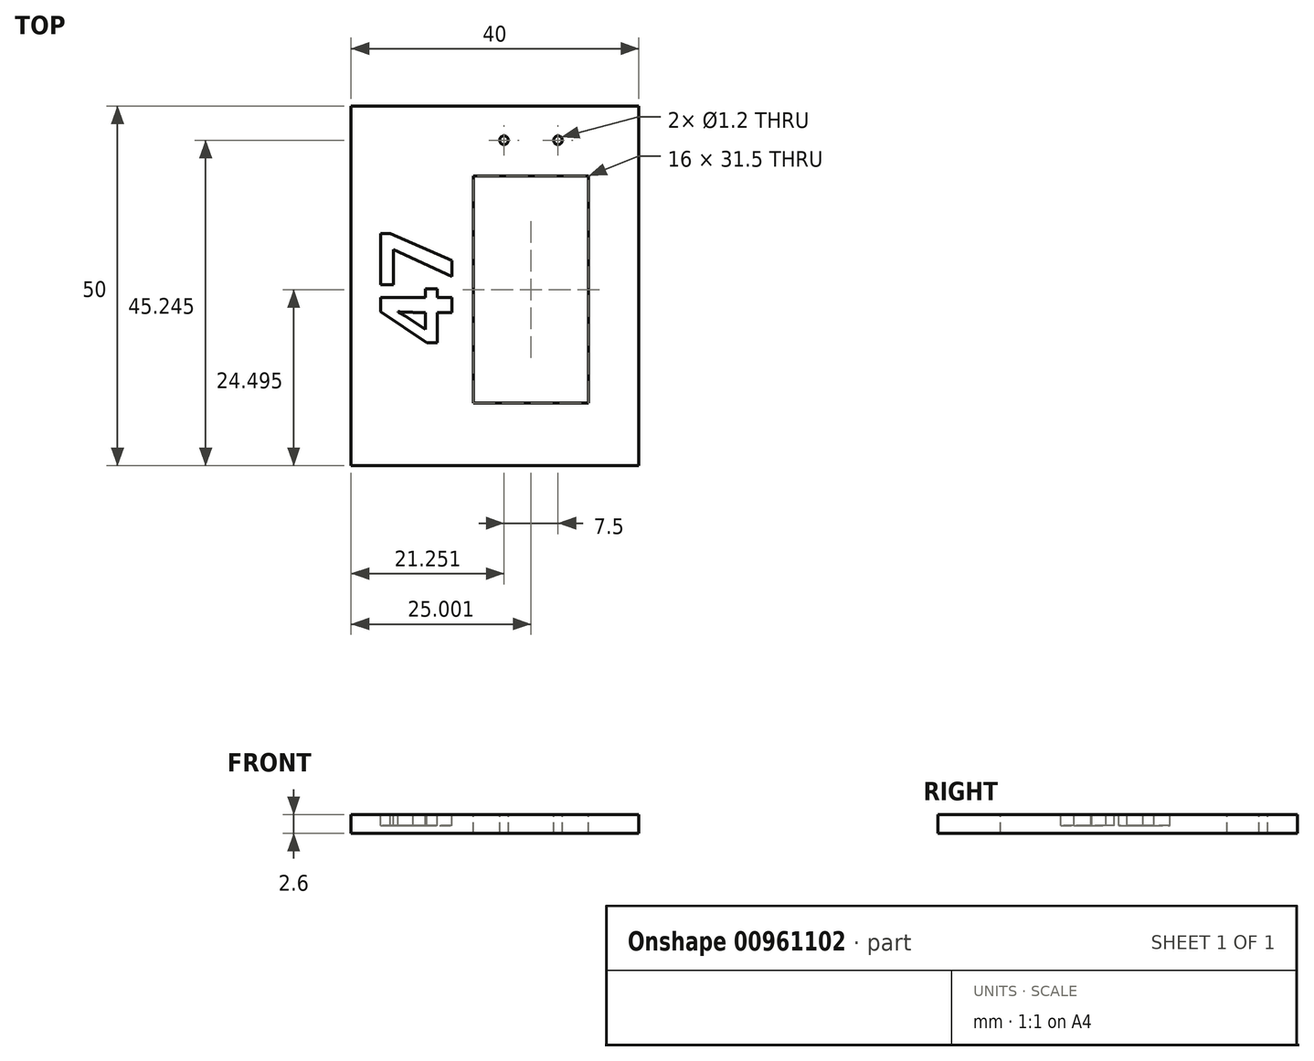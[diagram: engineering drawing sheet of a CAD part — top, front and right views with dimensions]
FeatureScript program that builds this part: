
annotation { "Feature Type Name" : "Feature", "Feature Type Description" : "" }
export const myFeature = defineFeature(function(context is Context, id is Id, definition is map)
    precondition{}
    {
        {
            var Q0;
            Q0=qCreatedBy(makeId("Top.planeOp"),FACE);
            var sketch = newSketch(context, id + "F0", { "sketchPlane" : qUnion([Q0])});
            skLineSegment(sketch, "E0.bottom", {"start": v(-43.16, 28.34) * mm, "end": v(-3.16, 28.34) * mm});
            skLineSegment(sketch, "E0.top", {"start": v(-43.16, -21.66) * mm, "end": v(-3.16, -21.66) * mm});
            skLineSegment(sketch, "E0.left", {"start": v(-43.16, 28.34) * mm, "end": v(-43.16, -21.66) * mm});
            skLineSegment(sketch, "E0.right", {"start": v(-3.16, 28.34) * mm, "end": v(-3.16, -21.66) * mm});
            skSolve(sketch);
        }
        {
            var Q0;
            Q0=makeQuery(id+"F0.imprint","IMPRINT",FACE,{"disambiguationData":[TD([[makeQuery(id+"F0.imprint","IMPRINT",EDGE,{"derivedFrom":sQuery(id+"F0.wireOp",EDGE,"E0.bottom")}),-1.0]])]});
            extrude(context, id + "F1", {"entities" : qUnion([Q0]), "depth" : 2.6 * mm, "offsetDistance" : 25 * mm});
        }
        {
            var Q0;
            Q0=makeQuery(id+"F1.opExtrude","CAP_FACE",FACE,{"disambiguationData":[OSD([sQuery(id+"F0.wireOp",EDGE,"E0.bottom"),sQuery(id+"F0.wireOp",EDGE,"E0.top"),sQuery(id+"F0.wireOp",EDGE,"E0.left"),sQuery(id+"F0.wireOp",EDGE,"E0.right")])],"isStart":false});
            var sketch = newSketch(context, id + "F2", { "sketchPlane" : qUnion([Q0])});
            skText(sketch, "E1", { "text": "47", "fontName": "OpenSans-Bold.ttf"});
            const initialGuessF2  = {"E1": [-0.02916, -0.00481, 0, 1, 0.01]};
            skSetInitialGuess(sketch, initialGuessF2);
            skSolve(sketch);
        }
        {
            var Q0;
            Q0=qSketchRegion(id+"F2",true);
            extrude(context, id + "F3", {"entities" : qUnion([Q0]), "operationType" : NewBodyOperationType.REMOVE, "oppositeDirection" : true, "depth" : 1.5 * mm, "offsetDistance" : 25 * mm});
        }
        {
            var Q0;
            {var subQ0=sQuery(id+"F0.wireOp",EDGE,"E0.left");var subQ1=sQuery(id+"F0.wireOp",EDGE,"E0.bottom");var subQ2=sQuery(id+"F0.wireOp",EDGE,"E0.right");var subQ3=sQuery(id+"F0.wireOp",EDGE,"E0.top");Q0=makeQuery(id+"F3.boolean.opBoolean","SPLIT",FACE,{"disambiguationData":[TD([makeQuery(id+"F1.opExtrude","SWEPT_FACE",FACE,{"disambiguationData":[OSD([subQ1])]})])],"derivedFrom":makeQuery(id+"F1.opExtrude","CAP_FACE",FACE,{"disambiguationData":[OSD([subQ1,subQ3,subQ0,subQ2])],"isStart":false})});}
            var sketch = newSketch(context, id + "F4", { "sketchPlane" : qUnion([Q0])});
            skLineSegment(sketch, "E2.bottom", {"start": v(-26.16, -12.91) * mm, "end": v(-10.16, -12.91) * mm});
            skLineSegment(sketch, "E2.top", {"start": v(-26.16, 18.59) * mm, "end": v(-10.16, 18.59) * mm});
            skLineSegment(sketch, "E2.left", {"start": v(-26.16, -12.91) * mm, "end": v(-26.16, 18.59) * mm});
            skLineSegment(sketch, "E2.right", {"start": v(-10.16, -12.91) * mm, "end": v(-10.16, 18.59) * mm});
            skCircle(sketch, "E3", {"center": v(-21.9, 23.59) * mm, "radius": 0.6 * mm});
            skCircle(sketch, "E4", {"center": v(-14.4, 23.59) * mm, "radius": 0.6 * mm});
            skSolve(sketch);
        }
        {
            var Q0;
            Q0 = qSketchRegion(id + "F4", true);
            extrude(context, id + "F5", {"entities" : qUnion([Q0]), "operationType" : NewBodyOperationType.REMOVE, "endBound" : BoundingType.UP_TO_NEXT, "oppositeDirection" : true, "depth" : 25 * mm, "offsetDistance" : 25 * mm});
        }
    });
